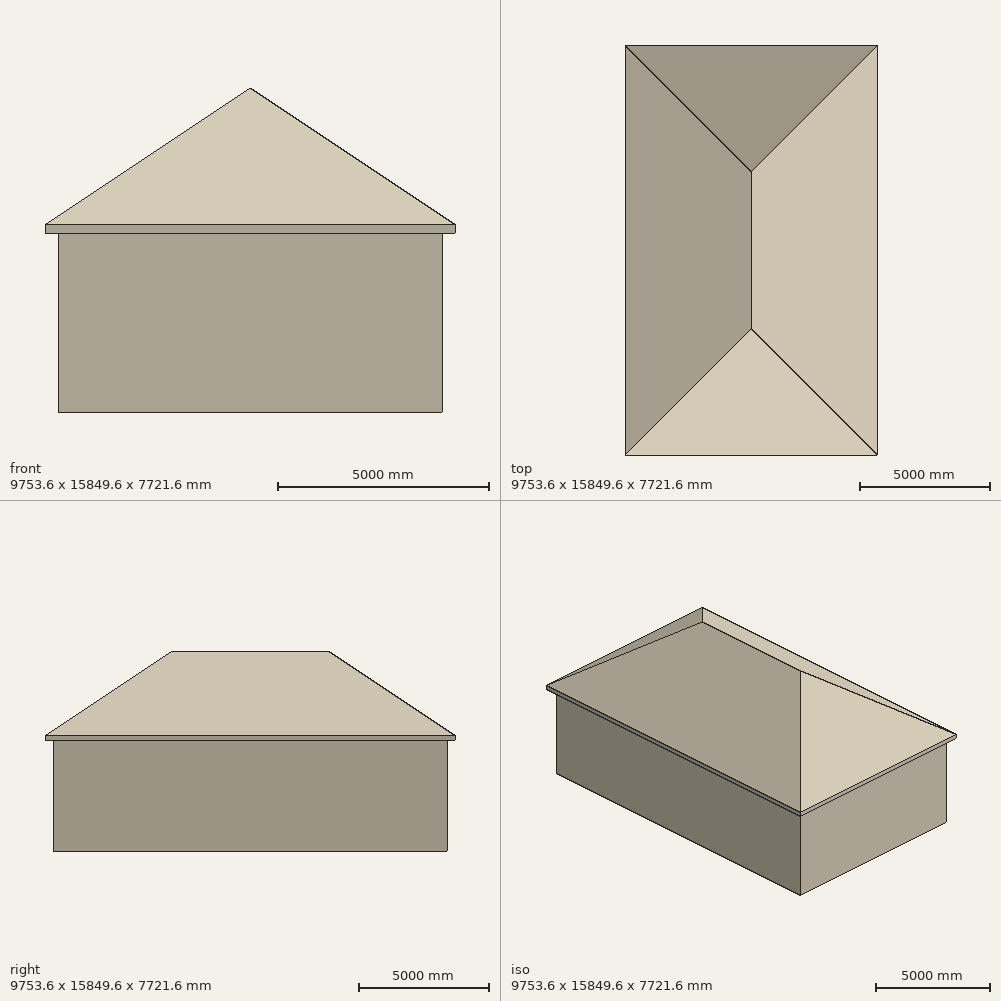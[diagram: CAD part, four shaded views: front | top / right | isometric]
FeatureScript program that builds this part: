
annotation { "Feature Type Name" : "Feature", "Feature Type Description" : "" }
export const myFeature = defineFeature(function(context is Context, id is Id, definition is map)
    precondition{}
    {
        {
            var Q0;
            Q0=qCreatedBy(makeId("Top.planeOp"),FACE);
            var sketch = newSketch(context, id + "F0", { "sketchPlane" : qUnion([Q0])});
            skLineSegment(sketch, "E0.bottom", {"start": v(0, 0) * mm, "end": v(9144, 0) * mm});
            skLineSegment(sketch, "E0.top", {"start": v(0, 15240) * mm, "end": v(9144, 15240) * mm});
            skLineSegment(sketch, "E0.left", {"start": v(0, 0) * mm, "end": v(0, 15240) * mm});
            skLineSegment(sketch, "E0.right", {"start": v(9144, 0) * mm, "end": v(9144, 15240) * mm});
            skSolve(sketch);
        }
        {
            var Q0;
            Q0=makeQuery(id+"F0.imprint","IMPRINT",FACE,{"disambiguationData":[TD([[makeQuery(id+"F0.imprint","IMPRINT",EDGE,{"derivedFrom":sQuery(id+"F0.wireOp",EDGE,"E0.bottom")}),1.0]])]});
            extrude(context, id + "F1", {"entities" : qUnion([Q0]), "depth" : 4267.2 * mm, "offsetDistance" : 25.4 * mm});
        }
        {
            var Q0;
            Q0=makeQuery(id+"F1.opExtrude","CAP_FACE",FACE,{"disambiguationData":[OSD([sQuery(id+"F0.wireOp",EDGE,"E0.bottom"),sQuery(id+"F0.wireOp",EDGE,"E0.top"),sQuery(id+"F0.wireOp",EDGE,"E0.left"),sQuery(id+"F0.wireOp",EDGE,"E0.right")])],"isStart":false});
            var sketch = newSketch(context, id + "F2", { "sketchPlane" : qUnion([Q0])});
            skLineSegment(sketch, "E1.bottom", {"start": v(-304.8, 15544.8) * mm, "end": v(9448.8, 15544.8) * mm});
            skLineSegment(sketch, "E1.top", {"start": v(-304.8, -304.8) * mm, "end": v(9448.8, -304.8) * mm});
            skLineSegment(sketch, "E1.left", {"start": v(-304.8, 15544.8) * mm, "end": v(-304.8, -304.8) * mm});
            skLineSegment(sketch, "E1.right", {"start": v(9448.8, 15544.8) * mm, "end": v(9448.8, -304.8) * mm});
            skSolve(sketch);
        }
        {
            var Q0;
            Q0 = qSketchRegion(id + "F2", true);
            extrude(context, id + "F3", {"entities" : qUnion([Q0]), "operationType" : NewBodyOperationType.ADD, "depth" : 6096 * mm, "offsetDistance" : 25.4 * mm});
        }
        {
            var Q0;
            Q0=makeQuery(id+"F3.opExtrude","SWEPT_FACE",FACE,{"disambiguationData":[OSD([sQuery(id+"F2.wireOp",EDGE,"E1.top")])]});
            var sketch = newSketch(context, id + "F4", { "sketchPlane" : qUnion([Q0])});
            skLineSegment(sketch, "E2.0", {"start": v(-304.8, 10363.2) * mm, "end": v(-304.8, 4267.2) * mm});
            skLineSegment(sketch, "E3.0", {"start": v(-304.8, 10363.2) * mm, "end": v(9448.8, 10363.2) * mm});
            skLineSegment(sketch, "E4.0", {"start": v(9448.8, 10363.2) * mm, "end": v(9448.8, 4267.2) * mm});
            skLineSegment(sketch, "E5", {"start": v(-304.8, 4470.4) * mm, "end": v(4572, 7721.6) * mm});
            skLineSegment(sketch, "E6", {"start": v(4572, 7721.6) * mm, "end": v(9448.8, 4470.4) * mm});
            skLineSegment(sketch, "E7", {"start": v(9448.8, 4470.4) * mm, "end": v(9144, 4470.4) * mm, "construction": true});
            skLineSegment(sketch, "E8", {"start": v(9144, 4470.4) * mm, "end": v(9144, 4673.6) * mm, "construction": true});
            skSolve(sketch);
        }
        {
            var Q0;
            Q0 = qSketchRegion(id + "F4", true);
            extrude(context, id + "F5", {"entities" : qUnion([Q0]), "operationType" : NewBodyOperationType.REMOVE, "endBound" : BoundingType.THROUGH_ALL, "oppositeDirection" : true, "depth" : 25.4 * mm, "offsetDistance" : 25.4 * mm});
        }
        {
            var Q0;
            Q0=makeQuery(id+"F3.opExtrude","SWEPT_FACE",FACE,{"disambiguationData":[OSD([sQuery(id+"F2.wireOp",EDGE,"E1.right")])]});
            var sketch = newSketch(context, id + "F6", { "sketchPlane" : qUnion([Q0])});
            skLineSegment(sketch, "E9.0", {"start": v(15544.8, 7721.6) * mm, "end": v(10668, 7721.6) * mm});
            skLineSegment(sketch, "E10.0", {"start": v(-304.8, 7721.6) * mm, "end": v(-304.8, 4470.4) * mm});
            skLineSegment(sketch, "E11.0", {"start": v(15544.8, 4470.4) * mm, "end": v(15544.8, 7721.6) * mm});
            skLineSegment(sketch, "E12", {"start": v(-304.8, 4470.4) * mm, "end": v(4572, 7721.6) * mm});
            skLineSegment(sketch, "E13", {"start": v(15544.8, 4470.4) * mm, "end": v(10668, 7721.6) * mm});
            skLineSegment(sketch, "E14.trimOffspring", {"start": v(4572, 7721.6) * mm, "end": v(-304.8, 7721.6) * mm});
            skLineSegment(sketch, "E15", {"start": v(-304.8, 4470.4) * mm, "end": v(0, 4470.4) * mm, "construction": true});
            skLineSegment(sketch, "E16", {"start": v(0, 4470.4) * mm, "end": v(0, 4673.6) * mm, "construction": true});
            skSolve(sketch);
        }
        {
            var Q0;
            Q0 = qSketchRegion(id + "F6", true);
            extrude(context, id + "F7", {"entities" : qUnion([Q0]), "operationType" : NewBodyOperationType.REMOVE, "endBound" : BoundingType.THROUGH_ALL, "oppositeDirection" : true, "depth" : 25.4 * mm, "offsetDistance" : 25.4 * mm});
        }
    });
